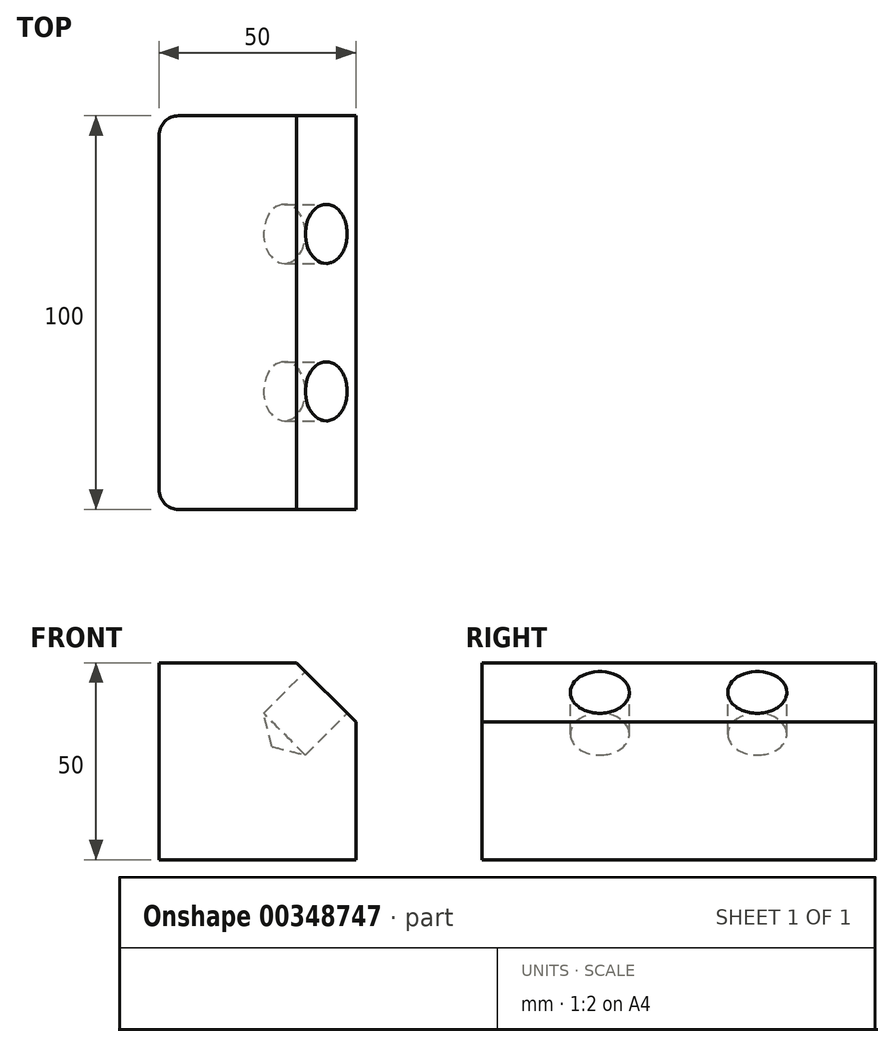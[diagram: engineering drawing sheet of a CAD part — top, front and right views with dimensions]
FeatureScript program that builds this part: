
annotation { "Feature Type Name" : "Feature", "Feature Type Description" : "" }
export const myFeature = defineFeature(function(context is Context, id is Id, definition is map)
    precondition{}
    {
        {
            var Q0;
            Q0=qCreatedBy(makeId("Top.planeOp"),FACE);
            var sketch = newSketch(context, id + "F0", { "sketchPlane" : qUnion([Q0])});
            skLineSegment(sketch, "E0.bottom", {"start": v(0, 0) * mm, "end": v(50, 0) * mm});
            skLineSegment(sketch, "E0.top", {"start": v(0, 100) * mm, "end": v(50, 100) * mm});
            skLineSegment(sketch, "E0.left", {"start": v(0, 0) * mm, "end": v(0, 100) * mm});
            skLineSegment(sketch, "E0.right", {"start": v(50, 0) * mm, "end": v(50, 100) * mm});
            skSolve(sketch);
        }
        {
            var Q0;
            Q0=makeQuery(id+"F0.imprint","IMPRINT",FACE,{"disambiguationData":[TD([[makeQuery(id+"F0.imprint","IMPRINT",EDGE,{"derivedFrom":sQuery(id+"F0.wireOp",EDGE,"E0.bottom")}),1.0]])]});
            extrude(context, id + "F1", {"entities" : qUnion([Q0]), "depth" : 50 * mm});
        }
        {
            var Q0;
            Q0=makeQuery(id+"F1.opExtrude","CAP_EDGE",EDGE,{"disambiguationData":[OSD([sQuery(id+"F0.wireOp",EDGE,"E0.right")])],"isStart":false});
            chamfer(context, id + "F2", {"entities" : qUnion([Q0]), "chamferType" : ChamferType.OFFSET_ANGLE, "width" : 15 * mm, "oppositeDirection" : false, "angle" : 45 * degree, "tangentPropagation" : true});
        }
        {
            var Q0;
            Q0=makeQuery(id+"F2.opChamfer","BLEND_FACE",FACE,{"disambiguationData":[OSD([sQuery(id+"F0.wireOp",EDGE,"E0.right")])]});
            var sketch = newSketch(context, id + "F3", { "sketchPlane" : qUnion([Q0])});
            skPoint(sketch, "E1", {"position": v(30, 0) * mm});
            skPoint(sketch, "E2", {"position": v(70, 0) * mm});
            skSolve(sketch);
        }
        {
            var Q0;
            Q0=sQuery(id+"F3.wireOp",VERTEX,"E1");
            var Q1;
            Q1=sQuery(id+"F3.wireOp",VERTEX,"E2");
            var Q2;
            Q2=makeQuery(id+"F1.opExtrude","SWEPT_BODY",BODY,{"disambiguationData":[OSD([sQuery(id+"F0.wireOp",EDGE,"E0.bottom"),sQuery(id+"F0.wireOp",EDGE,"E0.top"),sQuery(id+"F0.wireOp",EDGE,"E0.left"),sQuery(id+"F0.wireOp",EDGE,"E0.right")])]});
            hole(context, id + "F4", {"style" : HoleStyle.SIMPLE, "endStyle" : HoleEndStyle.BLIND, "holeDiameter" : 15 * mm, "holeDepth" : 15 * mm, "isTappedThrough" : true, "tappedDepth" : 12 * mm, "tapClearance" : 3, "locations" : qUnion([Q0, Q1]), "scope" : qUnion([Q2])});
        }
        {
            var Q0;
            Q0=makeQuery(id+"F1.opExtrude","SWEPT_EDGE",EDGE,{"disambiguationData":[OSD([sQuery(id+"F0.wireOp",EDGE,"E0.top"),sQuery(id+"F0.wireOp",EDGE,"E0.left")])]});
            fillet(context, id + "F5", {"entities" : qUnion([Q0]), "radius" : 5 * mm, "tangentPropagation" : true, "allowEdgeOverflow" : false});
        }
        {
            var Q0;
            Q0=makeQuery(id+"F1.opExtrude","SWEPT_EDGE",EDGE,{"disambiguationData":[OSD([sQuery(id+"F0.wireOp",EDGE,"E0.bottom"),sQuery(id+"F0.wireOp",EDGE,"E0.left")])]});
            fillet(context, id + "F6", {"entities" : qUnion([Q0]), "radius" : 5 * mm, "tangentPropagation" : true, "allowEdgeOverflow" : false});
        }
    });
